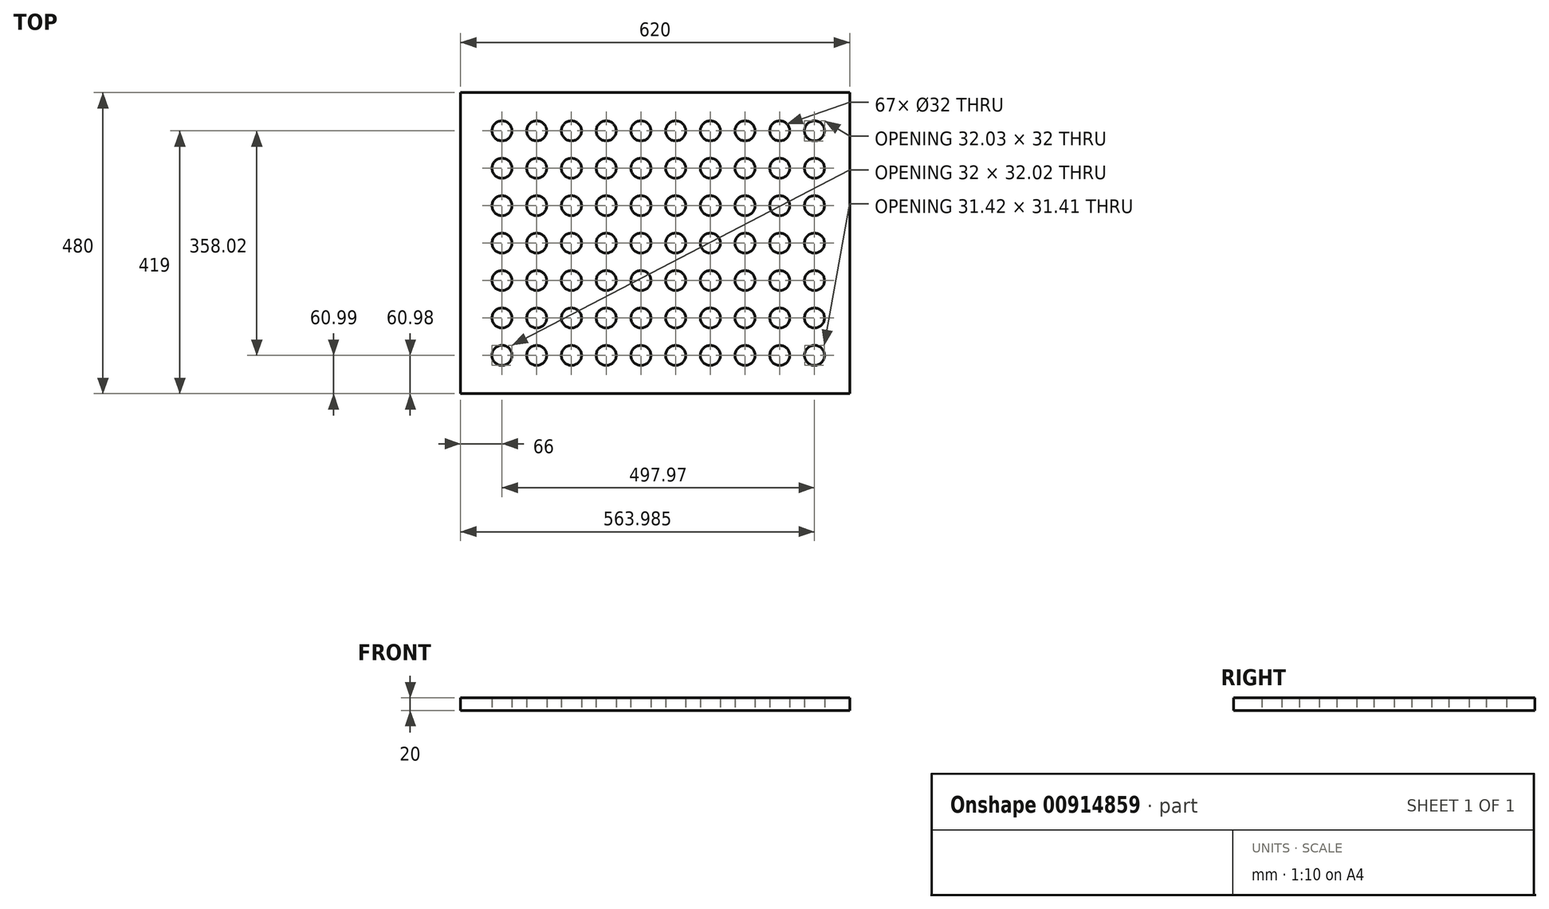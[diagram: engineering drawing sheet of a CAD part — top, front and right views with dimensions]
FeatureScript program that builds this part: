
annotation { "Feature Type Name" : "Feature", "Feature Type Description" : "" }
export const myFeature = defineFeature(function(context is Context, id is Id, definition is map)
    precondition{}
    {
        {
            var Q0;
            Q0=qCreatedBy(makeId("Top.planeOp"),FACE);
            var sketch = newSketch(context, id + "F0", { "sketchPlane" : qUnion([Q0])});
            skLineSegment(sketch, "E0.bottom", {"start": v(310, 240) * mm, "end": v(-310, 240) * mm});
            skLineSegment(sketch, "E0.top", {"start": v(310, -240) * mm, "end": v(-310, -240) * mm});
            skLineSegment(sketch, "E0.left", {"start": v(310, 240) * mm, "end": v(310, -240) * mm});
            skLineSegment(sketch, "E0.right", {"start": v(-310, 240) * mm, "end": v(-310, -240) * mm});
            skPoint(sketch, "E0.middle", {"position": v(0, 0) * mm});
            skCircle(sketch, "E1", {"center": v(-244, -179) * mm, "radius": 16 * mm});
            skCircle(sketch, "E2", {"center": v(254, -179) * mm, "radius": 16 * mm});
            skCircle(sketch, "E3", {"center": v(254, 179) * mm, "radius": 16 * mm});
            skCircle(sketch, "E4", {"center": v(-244, 179) * mm, "radius": 16 * mm});
            skCircle(sketch, "E5.0.1.0", {"center": v(-244, 119.33) * mm, "radius": 16 * mm});
            skCircle(sketch, "E5.0.2.0", {"center": v(-244, 59.66) * mm, "radius": 16 * mm});
            skCircle(sketch, "E5.0.3.0", {"center": v(-244, 0) * mm, "radius": 16 * mm});
            skCircle(sketch, "E5.0.4.0", {"center": v(-244, -59.68) * mm, "radius": 16 * mm});
            skCircle(sketch, "E5.1.0.0", {"center": v(-188.67, 179) * mm, "radius": 16 * mm});
            skCircle(sketch, "E5.1.1.0", {"center": v(-188.67, 119.33) * mm, "radius": 16 * mm});
            skCircle(sketch, "E5.1.2.0", {"center": v(-188.67, 59.66) * mm, "radius": 16 * mm});
            skCircle(sketch, "E5.1.3.0", {"center": v(-188.67, 0) * mm, "radius": 16 * mm});
            skCircle(sketch, "E5.1.4.0", {"center": v(-188.67, -59.68) * mm, "radius": 16 * mm});
            skCircle(sketch, "E5.2.0.0", {"center": v(-133.34, 179) * mm, "radius": 16 * mm});
            skCircle(sketch, "E5.2.1.0", {"center": v(-133.34, 119.33) * mm, "radius": 16 * mm});
            skCircle(sketch, "E5.2.2.0", {"center": v(-133.34, 59.66) * mm, "radius": 16 * mm});
            skCircle(sketch, "E5.2.3.0", {"center": v(-133.34, 0) * mm, "radius": 16 * mm});
            skCircle(sketch, "E5.2.4.0", {"center": v(-133.34, -59.68) * mm, "radius": 16 * mm});
            skCircle(sketch, "E5.3.0.0", {"center": v(-78.01, 179) * mm, "radius": 16 * mm});
            skCircle(sketch, "E5.3.1.0", {"center": v(-78.01, 119.33) * mm, "radius": 16 * mm});
            skCircle(sketch, "E5.3.2.0", {"center": v(-78.01, 59.66) * mm, "radius": 16 * mm});
            skCircle(sketch, "E5.3.3.0", {"center": v(-78.01, 0) * mm, "radius": 16 * mm});
            skCircle(sketch, "E5.3.4.0", {"center": v(-78.01, -59.68) * mm, "radius": 16 * mm});
            skCircle(sketch, "E5.4.0.0", {"center": v(-22.68, 179) * mm, "radius": 16 * mm});
            skCircle(sketch, "E5.4.1.0", {"center": v(-22.68, 119.33) * mm, "radius": 16 * mm});
            skCircle(sketch, "E5.4.2.0", {"center": v(-22.68, 59.66) * mm, "radius": 16 * mm});
            skCircle(sketch, "E5.4.3.0", {"center": v(-22.68, 0) * mm, "radius": 16 * mm});
            skCircle(sketch, "E5.4.4.0", {"center": v(-22.68, -59.68) * mm, "radius": 16 * mm});
            skCircle(sketch, "E5.5.0.0", {"center": v(32.65, 179) * mm, "radius": 16 * mm});
            skCircle(sketch, "E5.5.1.0", {"center": v(32.65, 119.33) * mm, "radius": 16 * mm});
            skCircle(sketch, "E5.5.2.0", {"center": v(32.65, 59.66) * mm, "radius": 16 * mm});
            skCircle(sketch, "E5.5.3.0", {"center": v(32.65, 0) * mm, "radius": 16 * mm});
            skCircle(sketch, "E5.5.4.0", {"center": v(32.65, -59.68) * mm, "radius": 16 * mm});
            skCircle(sketch, "E5.6.0.0", {"center": v(87.98, 179) * mm, "radius": 16 * mm});
            skCircle(sketch, "E5.6.1.0", {"center": v(87.98, 119.33) * mm, "radius": 16 * mm});
            skCircle(sketch, "E5.6.2.0", {"center": v(87.98, 59.66) * mm, "radius": 16 * mm});
            skCircle(sketch, "E5.6.3.0", {"center": v(87.98, 0) * mm, "radius": 16 * mm});
            skCircle(sketch, "E5.6.4.0", {"center": v(87.98, -59.68) * mm, "radius": 16 * mm});
            skCircle(sketch, "E5.7.0.0", {"center": v(143.3, 179) * mm, "radius": 16 * mm});
            skCircle(sketch, "E5.7.1.0", {"center": v(143.3, 119.33) * mm, "radius": 16 * mm});
            skCircle(sketch, "E5.7.2.0", {"center": v(143.3, 59.66) * mm, "radius": 16 * mm});
            skCircle(sketch, "E5.7.3.0", {"center": v(143.3, 0) * mm, "radius": 16 * mm});
            skCircle(sketch, "E5.7.4.0", {"center": v(143.3, -59.68) * mm, "radius": 16 * mm});
            skLineSegment(sketch, "E5.direction1", {"start": v(-244, 179) * mm, "end": v(-188.67, 179) * mm, "construction": true});
            skLineSegment(sketch, "E5.direction2", {"start": v(-244, 179) * mm, "end": v(-244, 119.33) * mm, "construction": true});
            skCircle(sketch, "E6.0.8.0", {"center": v(198.64, 179) * mm, "radius": 16 * mm});
            skCircle(sketch, "E6.0.8.1", {"center": v(198.64, 119.33) * mm, "radius": 16 * mm});
            skCircle(sketch, "E6.0.8.2", {"center": v(198.64, 59.66) * mm, "radius": 16 * mm});
            skCircle(sketch, "E6.0.8.3", {"center": v(198.64, 0) * mm, "radius": 16 * mm});
            skCircle(sketch, "E6.0.8.4", {"center": v(198.64, -59.68) * mm, "radius": 16 * mm});
            skCircle(sketch, "E6.0.9.0", {"center": v(253.97, 179) * mm, "radius": 16 * mm});
            skCircle(sketch, "E6.0.9.1", {"center": v(253.97, 119.33) * mm, "radius": 16 * mm});
            skCircle(sketch, "E6.0.9.2", {"center": v(253.97, 59.66) * mm, "radius": 16 * mm});
            skCircle(sketch, "E6.0.9.3", {"center": v(253.97, 0) * mm, "radius": 16 * mm});
            skCircle(sketch, "E6.0.9.4", {"center": v(253.97, -59.68) * mm, "radius": 16 * mm});
            skCircle(sketch, "E7.0.0.5", {"center": v(-244, -119.35) * mm, "radius": 16 * mm});
            skCircle(sketch, "E7.0.0.6", {"center": v(-244, -179.02) * mm, "radius": 16 * mm});
            skCircle(sketch, "E7.0.1.5", {"center": v(-188.67, -119.35) * mm, "radius": 16 * mm});
            skCircle(sketch, "E7.0.1.6", {"center": v(-188.67, -179.02) * mm, "radius": 16 * mm});
            skCircle(sketch, "E7.0.2.5", {"center": v(-133.34, -119.35) * mm, "radius": 16 * mm});
            skCircle(sketch, "E7.0.2.6", {"center": v(-133.34, -179.02) * mm, "radius": 16 * mm});
            skCircle(sketch, "E7.0.3.5", {"center": v(-78.01, -119.35) * mm, "radius": 16 * mm});
            skCircle(sketch, "E7.0.3.6", {"center": v(-78.01, -179.02) * mm, "radius": 16 * mm});
            skCircle(sketch, "E7.0.4.5", {"center": v(-22.68, -119.35) * mm, "radius": 16 * mm});
            skCircle(sketch, "E7.0.4.6", {"center": v(-22.68, -179.02) * mm, "radius": 16 * mm});
            skCircle(sketch, "E7.0.5.5", {"center": v(32.65, -119.35) * mm, "radius": 16 * mm});
            skCircle(sketch, "E7.0.5.6", {"center": v(32.65, -179.02) * mm, "radius": 16 * mm});
            skCircle(sketch, "E7.0.6.5", {"center": v(87.98, -119.35) * mm, "radius": 16 * mm});
            skCircle(sketch, "E7.0.6.6", {"center": v(87.98, -179.02) * mm, "radius": 16 * mm});
            skCircle(sketch, "E7.0.7.5", {"center": v(143.3, -119.35) * mm, "radius": 16 * mm});
            skCircle(sketch, "E7.0.7.6", {"center": v(143.3, -179.02) * mm, "radius": 16 * mm});
            skCircle(sketch, "E7.0.8.5", {"center": v(198.64, -119.35) * mm, "radius": 16 * mm});
            skCircle(sketch, "E7.0.8.6", {"center": v(198.64, -179.02) * mm, "radius": 16 * mm});
            skCircle(sketch, "E7.0.9.5", {"center": v(253.97, -119.35) * mm, "radius": 16 * mm});
            skCircle(sketch, "E7.0.9.6", {"center": v(253.97, -179.02) * mm, "radius": 16 * mm});
            skSolve(sketch);
        }
        {
            var Q0;
            Q0=makeQuery(id+"F0.imprint","IMPRINT",FACE,{"disambiguationData":[TD([[makeQuery(id+"F0.imprint","IMPRINT",EDGE,{"derivedFrom":sQuery(id+"F0.wireOp",EDGE,"E0.bottom")}),1.0]])]});
            extrude(context, id + "F1", {"entities" : qUnion([Q0]), "depth" : 20 * mm, "offsetDistance" : 25 * mm});
        }
    });
